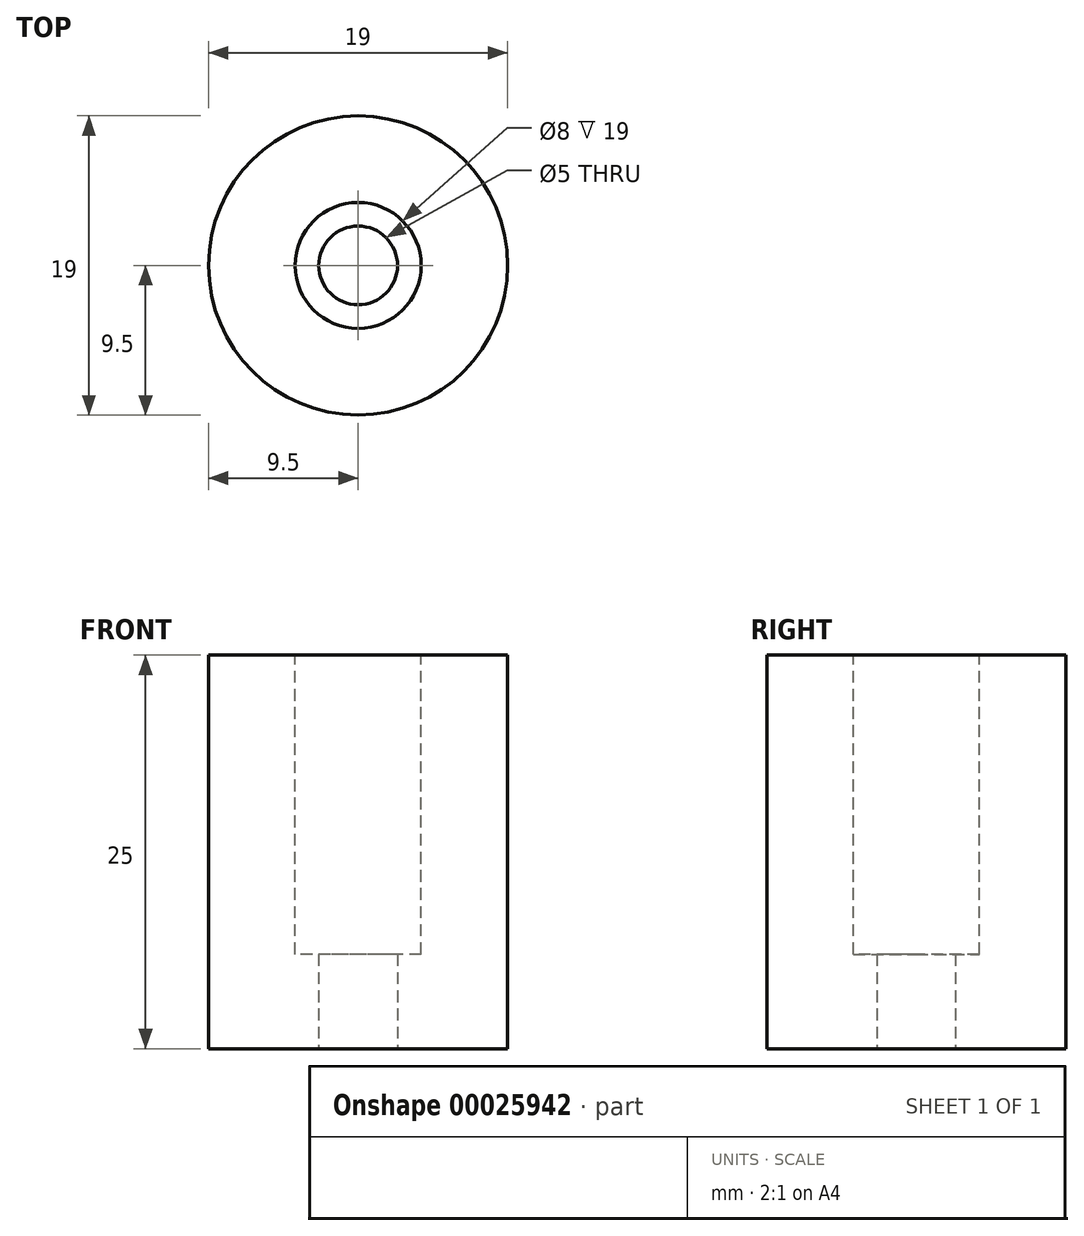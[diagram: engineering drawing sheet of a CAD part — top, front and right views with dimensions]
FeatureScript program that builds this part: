
annotation { "Feature Type Name" : "Feature", "Feature Type Description" : "" }
export const myFeature = defineFeature(function(context is Context, id is Id, definition is map)
    precondition{}
    {
        {
            var Q0;
            Q0=qCreatedBy(makeId("Top.planeOp"),FACE);
            var sketch = newSketch(context, id + "F0", { "sketchPlane" : qUnion([Q0])});
            skCircle(sketch, "E0", {"center": v(0, 0) * mm, "radius": 9.5 * mm});
            skSolve(sketch);
        }
        {
            var Q0;
            Q0=makeQuery(id+"F0.imprint","IMPRINT",FACE,{"disambiguationData":[TD([[makeQuery(id+"F0.imprint","IMPRINT",EDGE,{"derivedFrom":sQuery(id+"F0.wireOp",EDGE,"E0")}),1.0]])]});
            extrude(context, id + "F1", {"entities" : qUnion([Q0]), "depth" : 25 * mm});
        }
        {
            var Q0;
            Q0=makeQuery(id+"F1.opExtrude","CAP_FACE",FACE,{"disambiguationData":[OSD([sQuery(id+"F0.wireOp",EDGE,"E0")])],"isStart":false});
            var sketch = newSketch(context, id + "F2", { "sketchPlane" : qUnion([Q0])});
            skCircle(sketch, "E1", {"center": v(0, 0) * mm, "radius": 4 * mm});
            skSolve(sketch);
        }
        {
            var Q0;
            Q0 = qSketchRegion(id + "F2", true);
            extrude(context, id + "F3", {"entities" : qUnion([Q0]), "operationType" : NewBodyOperationType.REMOVE, "oppositeDirection" : true, "depth" : 19 * mm});
        }
        {
            var Q0;
            Q0=makeQuery(id+"F1.opExtrude","CAP_FACE",FACE,{"disambiguationData":[OSD([sQuery(id+"F0.wireOp",EDGE,"E0")])],"isStart":true});
            var sketch = newSketch(context, id + "F4", { "sketchPlane" : qUnion([Q0])});
            skCircle(sketch, "E2", {"center": v(0, 0) * mm, "radius": 2.5 * mm});
            skSolve(sketch);
        }
        {
            var Q0;
            Q0=makeQuery(id+"F4.imprint","IMPRINT",FACE,{"disambiguationData":[TD([[makeQuery(id+"F4.imprint","IMPRINT",EDGE,{"derivedFrom":sQuery(id+"F4.wireOp",EDGE,"E2")}),1.0]])]});
            extrude(context, id + "F5", {"entities" : qUnion([Q0]), "operationType" : NewBodyOperationType.REMOVE, "endBound" : BoundingType.THROUGH_ALL, "oppositeDirection" : true, "depth" : 25 * mm});
        }
    });
